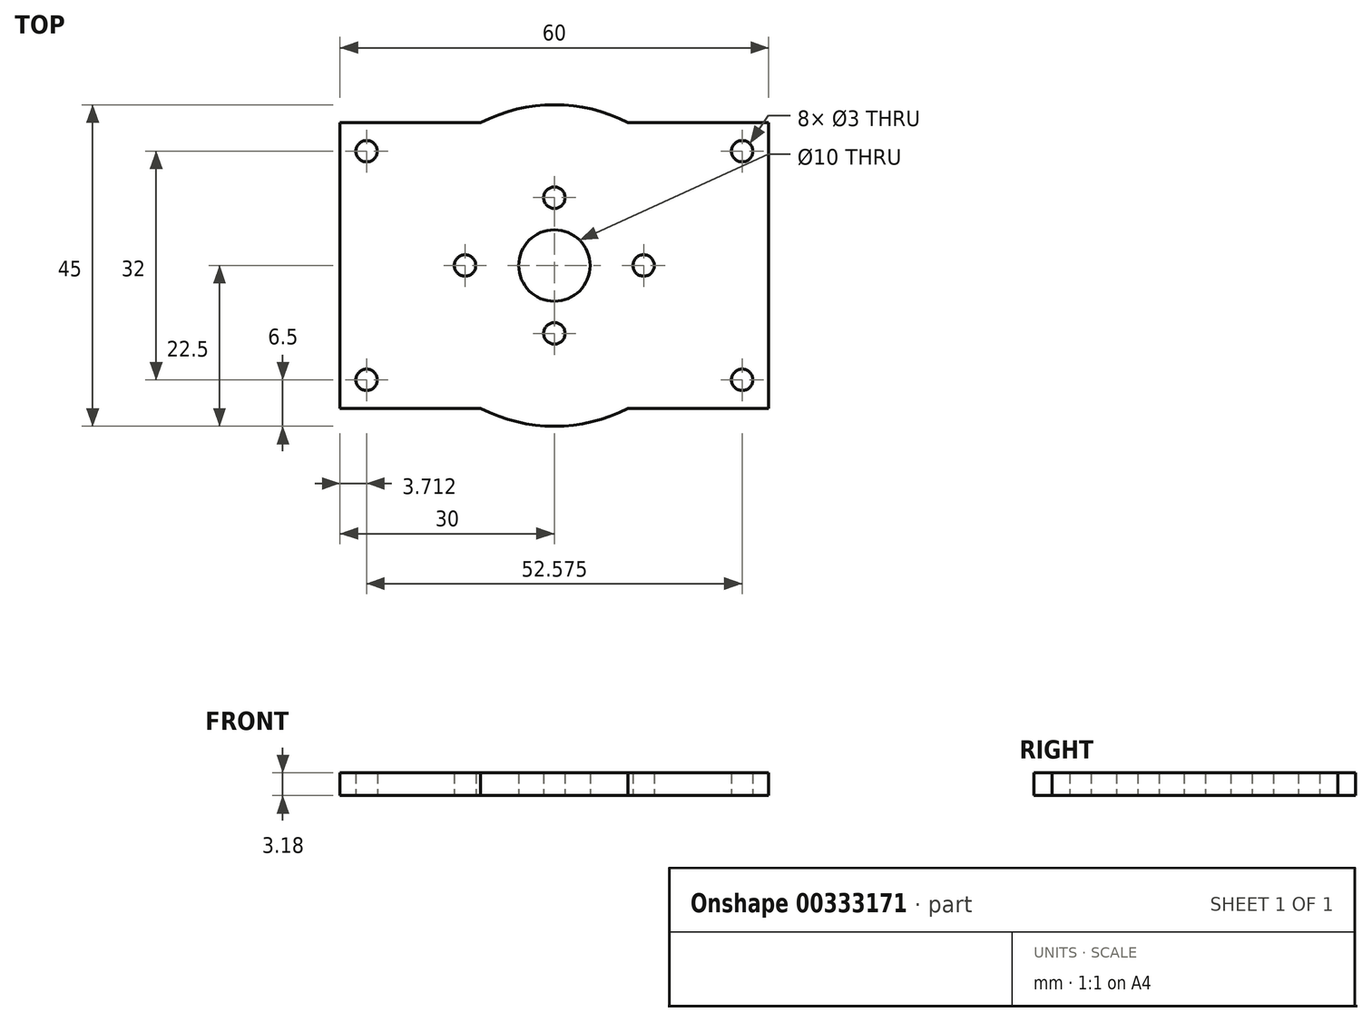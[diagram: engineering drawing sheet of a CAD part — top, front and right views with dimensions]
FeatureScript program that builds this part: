
annotation { "Feature Type Name" : "Feature", "Feature Type Description" : "" }
export const myFeature = defineFeature(function(context is Context, id is Id, definition is map)
    precondition{}
    {
        {
            var Q0;
            Q0=qCreatedBy(makeId("Top.planeOp"),FACE);
            var sketch = newSketch(context, id + "F0", { "sketchPlane" : qUnion([Q0])});
            skLineSegment(sketch, "E0.bottom", {"start": v(30, -20) * mm, "end": v(-30, -20) * mm});
            skLineSegment(sketch, "E0.top", {"start": v(30, 20) * mm, "end": v(-30, 20) * mm});
            skLineSegment(sketch, "E0.left", {"start": v(30, -20) * mm, "end": v(30, 20) * mm});
            skLineSegment(sketch, "E0.right", {"start": v(-30, -20) * mm, "end": v(-30, 20) * mm});
            skPoint(sketch, "E0.middle", {"position": v(0, 0) * mm});
            skCircle(sketch, "E1", {"center": v(0, 0) * mm, "radius": 22.5 * mm});
            skCircle(sketch, "E2", {"center": v(-26.29, 16) * mm, "radius": 1.5 * mm});
            skCircle(sketch, "E3.MirrorC", {"center": v(-26.29, -16) * mm, "radius": 1.5 * mm});
            skCircle(sketch, "E4.MirrorC", {"center": v(26.29, 16) * mm, "radius": 1.5 * mm});
            skCircle(sketch, "E5.MirrorC", {"center": v(26.29, -16) * mm, "radius": 1.5 * mm});
            skCircle(sketch, "E6", {"center": v(0, 0) * mm, "radius": 5 * mm});
            skCircle(sketch, "E7", {"center": v(0, 9.5) * mm, "radius": 1.5 * mm});
            skCircle(sketch, "E8.MirrorC", {"center": v(0, -9.5) * mm, "radius": 1.5 * mm});
            skCircle(sketch, "E9", {"center": v(-12.5, 0) * mm, "radius": 1.5 * mm});
            skCircle(sketch, "E10.MirrorC", {"center": v(12.5, 0) * mm, "radius": 1.5 * mm});
            skSolve(sketch);
        }
        {
            var Q0;
            Q0=qSketchRegion(id+"F0",true);
            extrude(context, id + "F1", {"entities" : qUnion([Q0]), "depth" : 3.17 * mm});
        }
    });
